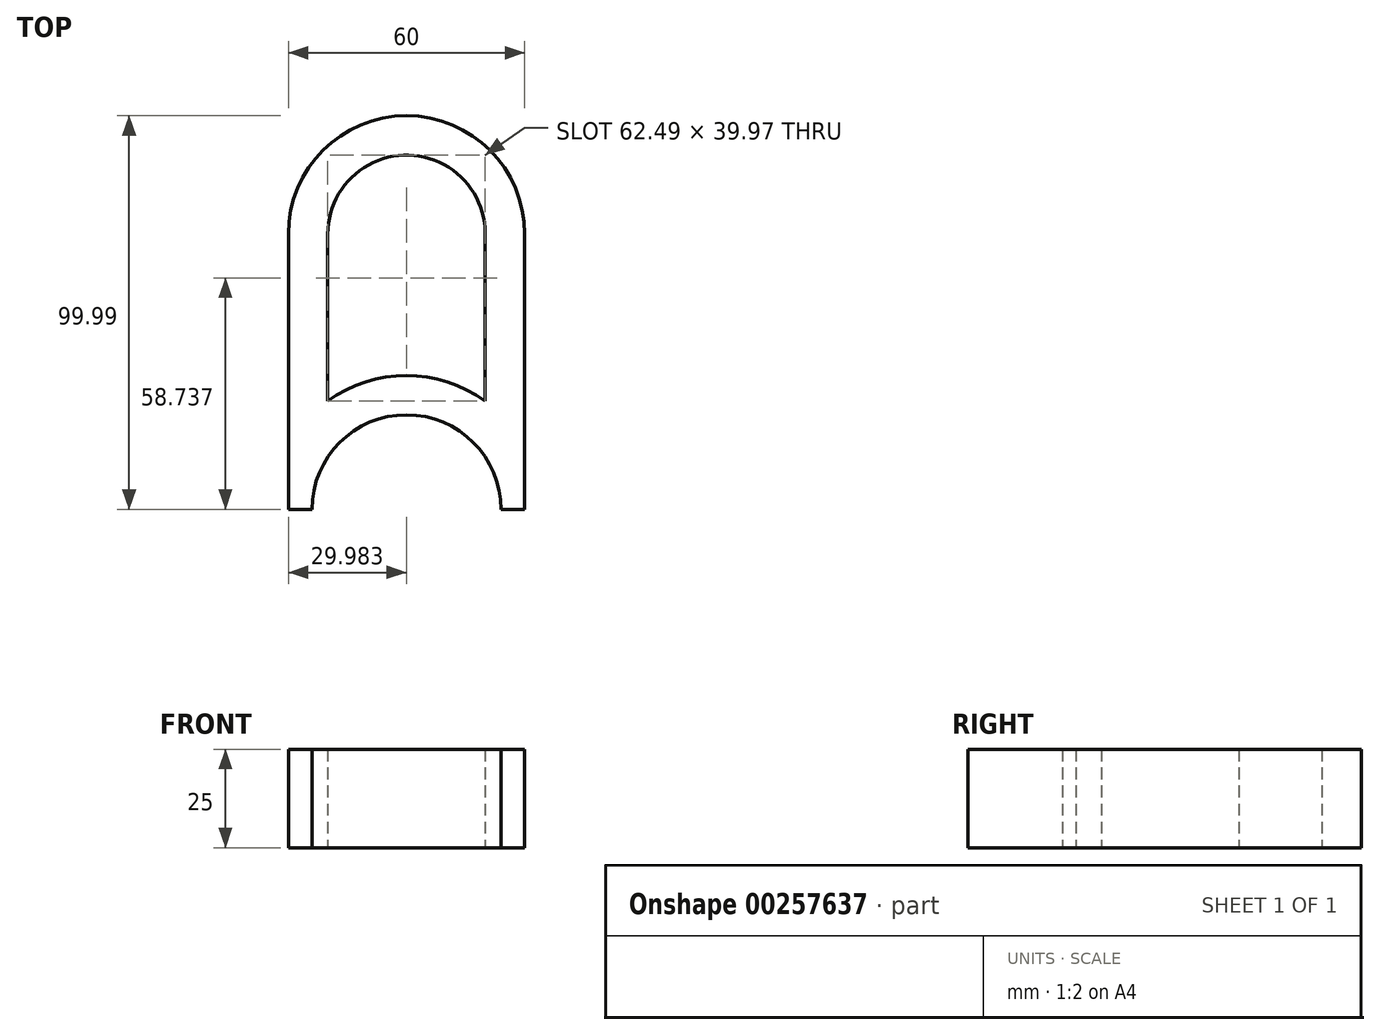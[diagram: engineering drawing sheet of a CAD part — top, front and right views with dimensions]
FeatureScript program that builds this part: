
annotation { "Feature Type Name" : "Feature", "Feature Type Description" : "" }
export const myFeature = defineFeature(function(context is Context, id is Id, definition is map)
    precondition{}
    {
        {
            var Q0;
            Q0=qCreatedBy(makeId("Top.planeOp"),FACE);
            var sketch = newSketch(context, id + "F0", { "sketchPlane" : qUnion([Q0])});
            skArc(sketch, "E0", {"start": v(30, 21.65) * mm, "mid": v(0, 51.65) * mm, "end": v(-30, 21.65) * mm});
            skArc(sketch, "E1", {"start": v(19.97, 20.5) * mm, "mid": v(0.58, 41.64) * mm, "end": v(-20, 21.65) * mm});
            skLineSegment(sketch, "E2", {"start": v(19.97, 22.8) * mm, "end": v(19.97, -20.82) * mm});
            skLineSegment(sketch, "E3", {"start": v(-20, 21.65) * mm, "end": v(-20, -20.85) * mm});
            skLineSegment(sketch, "E4", {"start": v(-30, 21.65) * mm, "end": v(-30, -48.34) * mm});
            skPoint(sketch, "E5.start.orphan", {"position": v(0, 51.65) * mm});
            skLineSegment(sketch, "E6", {"start": v(30, 21.65) * mm, "end": v(30, -48.34) * mm});
            skLineSegment(sketch, "E7", {"start": v(30, -48.34) * mm, "end": v(24, -48.34) * mm});
            skArc(sketch, "E8", {"start": v(24, -48.34) * mm, "mid": v(0, -24.34) * mm, "end": v(-24, -48.34) * mm});
            skArc(sketch, "E9", {"start": v(19.97, -20.82) * mm, "mid": v(-0.02, -14.34) * mm, "end": v(-20, -20.85) * mm});
            skLineSegment(sketch, "E10.trimOffspring", {"start": v(-24, -48.34) * mm, "end": v(-30, -48.34) * mm});
            skSolve(sketch);
        }
        {
            var Q0;
            Q0=makeQuery(id+"F0.imprint","IMPRINT",FACE,{"disambiguationData":[TD([[makeQuery(id+"F0.imprint","IMPRINT",EDGE,{"derivedFrom":sQuery(id+"F0.wireOp",EDGE,"E0")}),1.0]])]});
            extrude(context, id + "F1", {"entities" : qUnion([Q0]), "depth" : 25 * mm});
        }
    });
